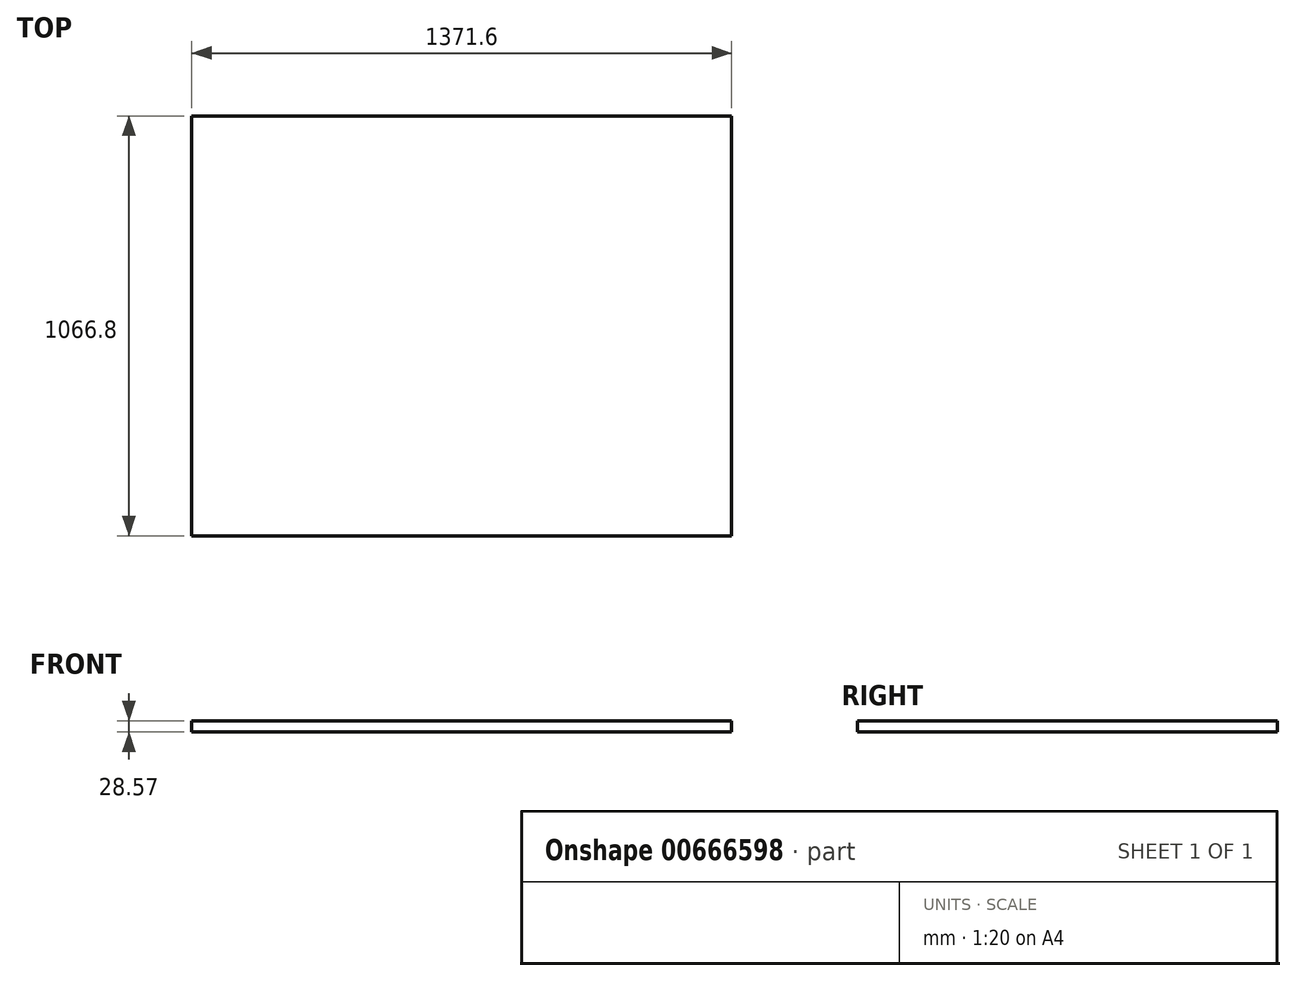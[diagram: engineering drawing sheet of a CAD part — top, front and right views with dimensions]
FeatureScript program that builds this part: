
annotation { "Feature Type Name" : "Feature", "Feature Type Description" : "" }
export const myFeature = defineFeature(function(context is Context, id is Id, definition is map)
    precondition{}
    {
        {
            var Q0;
            Q0=qCreatedBy(makeId("Top.planeOp"),FACE);
            var sketch = newSketch(context, id + "F0", { "sketchPlane" : qUnion([Q0])});
            skLineSegment(sketch, "E0.bottom", {"start": v(685.8, 533.4) * mm, "end": v(-685.8, 533.4) * mm});
            skLineSegment(sketch, "E0.top", {"start": v(685.8, -533.4) * mm, "end": v(-685.8, -533.4) * mm});
            skLineSegment(sketch, "E0.left", {"start": v(685.8, 533.4) * mm, "end": v(685.8, -533.4) * mm});
            skLineSegment(sketch, "E0.right", {"start": v(-685.8, 533.4) * mm, "end": v(-685.8, -533.4) * mm});
            skPoint(sketch, "E0.middle", {"position": v(0, 0) * mm});
            skSolve(sketch);
        }
        {
            var Q0;
            Q0=makeQuery(id+"F0.imprint","IMPRINT",FACE,{"disambiguationData":[TD([[makeQuery(id+"F0.imprint","IMPRINT",EDGE,{"derivedFrom":sQuery(id+"F0.wireOp",EDGE,"E0.bottom")}),1.0]])]});
            extrude(context, id + "F1", {"entities" : qUnion([Q0]), "depth" : 28.57 * mm, "offsetDistance" : 25.4 * mm});
        }
    });
